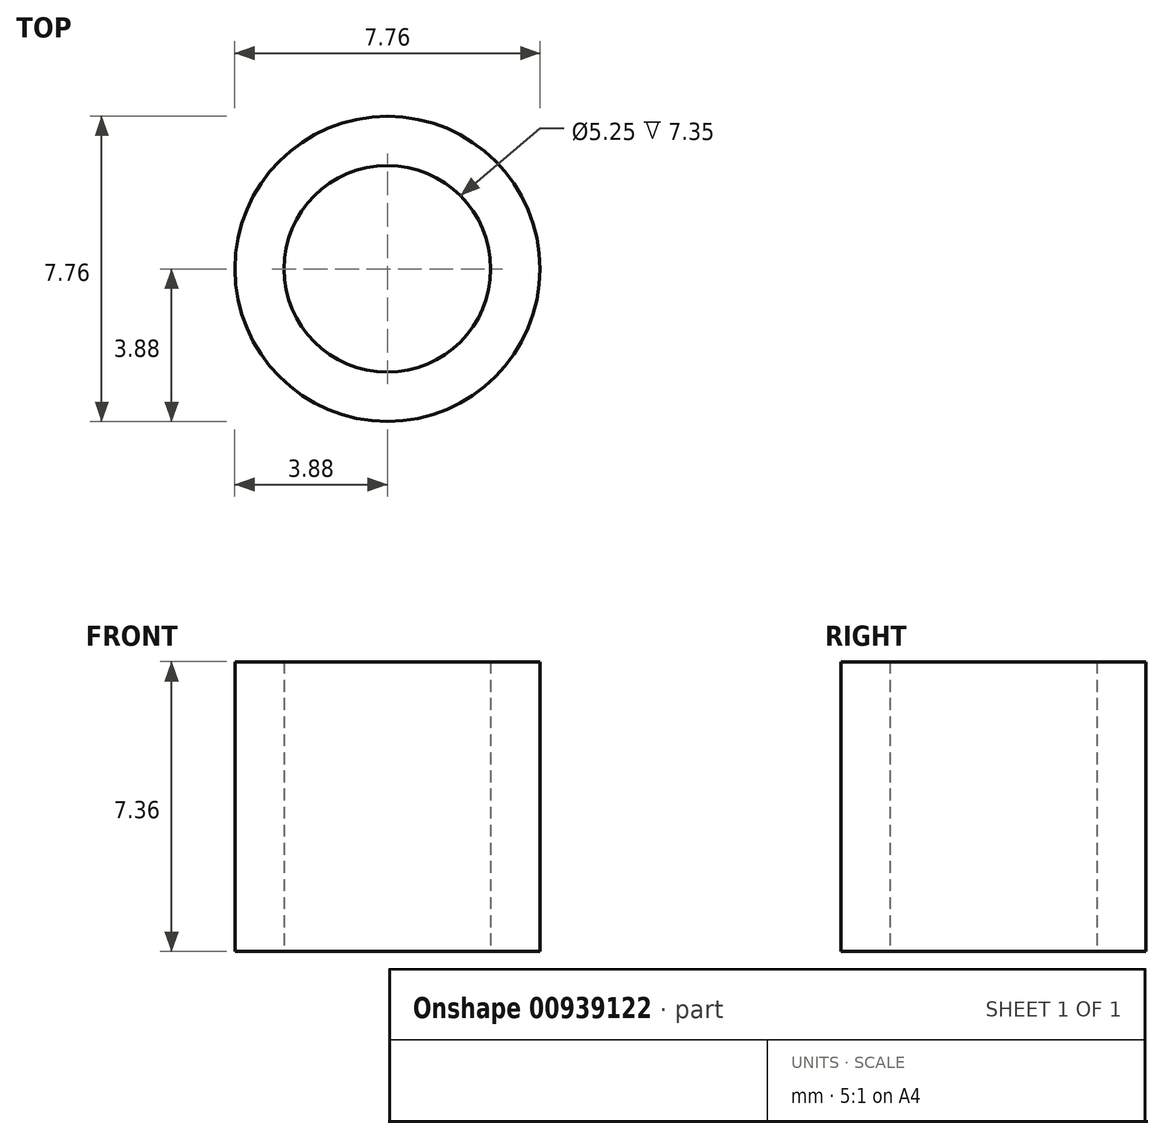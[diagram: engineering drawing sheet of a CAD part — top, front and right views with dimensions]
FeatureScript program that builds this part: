
annotation { "Feature Type Name" : "Feature", "Feature Type Description" : "" }
export const myFeature = defineFeature(function(context is Context, id is Id, definition is map)
    precondition{}
    {
        {
            var Q0;
            Q0=qCreatedBy(makeId("Top.planeOp"),FACE);
            var sketch = newSketch(context, id + "F0", { "sketchPlane" : qUnion([Q0])});
            skCircle(sketch, "E0", {"center": v(0, 0) * mm, "radius": 3.88 * mm});
            skCircle(sketch, "E1", {"center": v(0, 0) * mm, "radius": 2.62 * mm});
            skSolve(sketch);
        }
        {
            var Q0;
            Q0 = qSketchRegion(id + "F0", true);
            extrude(context, id + "F1", {"entities" : qUnion([Q0]), "endBound" : BoundingType.SYMMETRIC, "depth" : 7.35 * mm, "offsetDistance" : 25 * mm});
        }
    });
